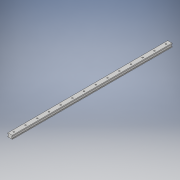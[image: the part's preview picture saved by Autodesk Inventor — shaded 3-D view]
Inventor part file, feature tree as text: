
AUTODESK INVENTOR PART (.ipt)
format: ipt  version: 2017 (Build 210142000, 142)  size: 174,592 bytes
history: native  units: in
note: dims shown in document units (in); Inventor stores cm internally (conversion verified against a paired STEP export)
features: sketch x7, extrude x1, hole x1
ambient origin geometry x8: Origin, YZ Plane, XZ Plane, XY Plane, X Axis, Y Axis, Z Axis, Center Point
bodies: Solid1 (feature_tree)
feature tree (9):
  sketch  "Sketch1"  dims[d6=0.0785in d7=29.03in d8=0.0in]
  extrude  "Extrusion1"  Depth=29.03in TaperAngle=0.0deg
  hole  "Hole1"  [1 undecoded]
  sketch  "Sketch4"  dims[d20=2.1295in]
  sketch  "Sketch5"  dims[d21=2.1295in]
  sketch  "Sketch6"  dims[d22=2.1295in]
  sketch  "Sketch7"  dims[d23=2.1295in d24=2.1295in d25=2.1295in d26=2.1295in d27=2.1295in d28=0.67in d29=2.1295in d30=2.1295in d31=2.1295in d33=0.3945in d34=0.3945in d35=0.3945in d36=0.3945in d37=0.3945in d38=0.235in d39=0.75in d40=0.375in d41=0.25in d42=0.5635in d43=1.0in d44=0.8108in d50=2.13in d59=0.3945in d60=0.3945in d61=2.13in d62=2.13in d63=0.3945in d64=2.13in d65=0.3945in d66=2.13in d67=2.13in d68=2.13in d69=2.13in d70=2.13in d71=2.13in d74=2.13in d75=2.13in d76=0.67in d77=0.3945in d78=0.3945in d79=0.3945in d80=0.3945in d81=0.3945in d82=2.13in d83=2.13in d84=0.3945in d85=0.3945in d86=0.3945in d18=1.0in d87=1.0in d88=1.0in]
  sketch  "Sketch2"  dims[d16=0.789in d17=2.1295in]
  sketch  "Sketch3"  dims[d19=2.1295in]
note: 1 required parameter value undecoded (feature->parameter linkage not recoverable at this tier; creation-order binding heuristic only, values carry confidence <= 0.55)
